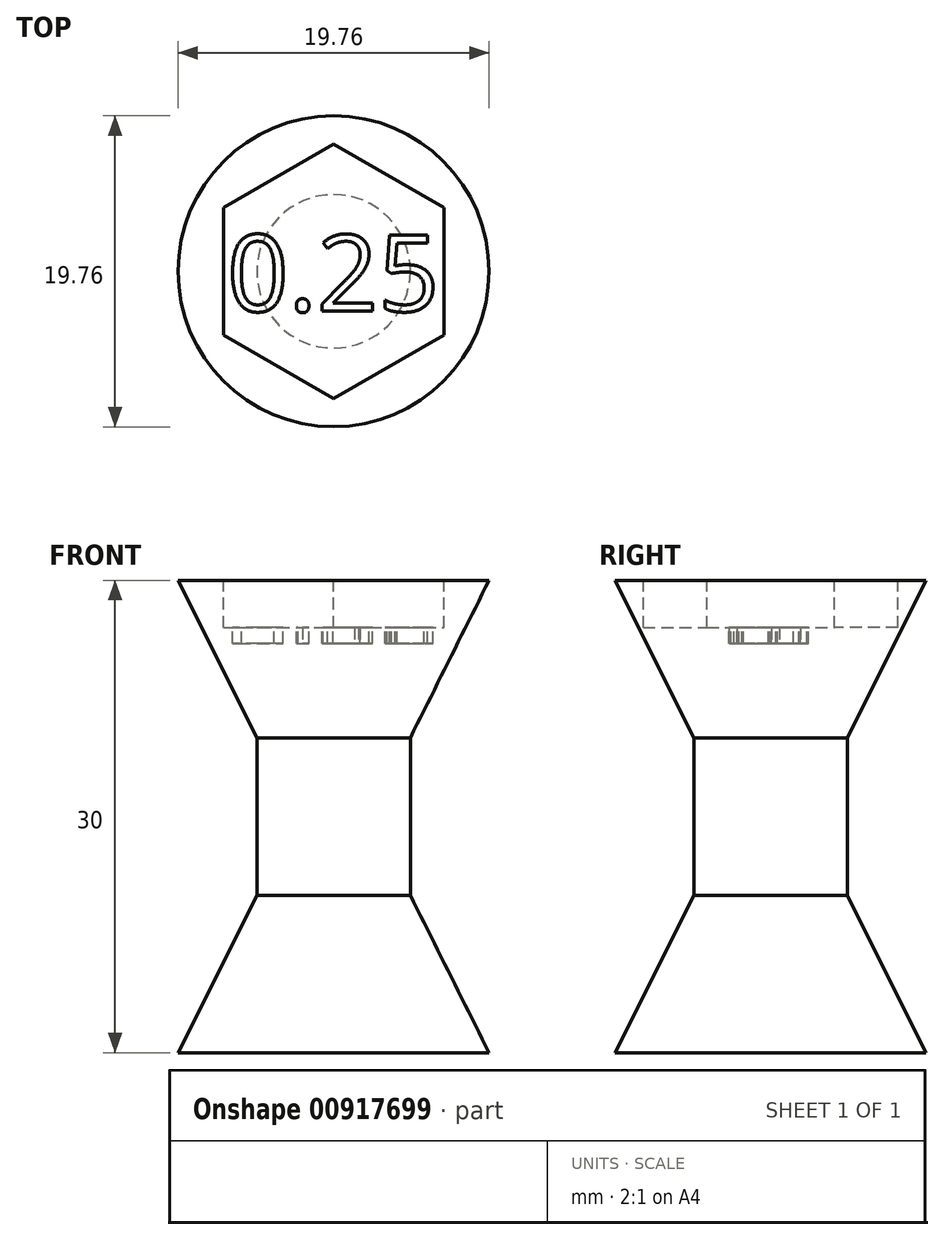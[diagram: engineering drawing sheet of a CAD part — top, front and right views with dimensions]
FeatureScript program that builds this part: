
annotation { "Feature Type Name" : "Feature", "Feature Type Description" : "" }
export const myFeature = defineFeature(function(context is Context, id is Id, definition is map)
    precondition{}
    {
        {
            var Q0;
            Q0=qCreatedBy(makeId("Front.planeOp"),FACE);
            var sketch = newSketch(context, id + "F0", { "sketchPlane" : qUnion([Q0])});
            skLineSegment(sketch, "E0", {"start": v(0, 15) * mm, "end": v(0, -15) * mm});
            skLineSegment(sketch, "E1", {"start": v(0, -15) * mm, "end": v(9.88, -15) * mm});
            skLineSegment(sketch, "E2", {"start": v(9.88, -15) * mm, "end": v(4.88, -5) * mm});
            skLineSegment(sketch, "E3", {"start": v(4.88, -5) * mm, "end": v(4.88, 5) * mm});
            skLineSegment(sketch, "E4", {"start": v(4.87, 5) * mm, "end": v(9.87, 15) * mm});
            skLineSegment(sketch, "E5", {"start": v(9.87, 15) * mm, "end": v(0, 15) * mm});
            skSolve(sketch);
        }
        {
            var Q0;
            Q0=makeQuery(id+"F0.imprint","IMPRINT",FACE,{"disambiguationData":[TD([[makeQuery(id+"F0.imprint","IMPRINT",EDGE,{"derivedFrom":sQuery(id+"F0.wireOp",EDGE,"E0")}),1.0]])]});
            var Q1;
            Q1=sQuery(id+"F0.wireOp",EDGE,"E0");
            var Q2;
            Q2=sQuery(id+"F0.wireOp",EDGE,"E1");
            var Q3;
            Q3=sQuery(id+"F0.wireOp",EDGE,"E2");
            var Q4;
            Q4=sQuery(id+"F0.wireOp",EDGE,"E3");
            var Q5;
            Q5=sQuery(id+"F0.wireOp",EDGE,"E4");
            var Q6;
            Q6=sQuery(id+"F0.wireOp",EDGE,"E5");
            var Q7;
            Q7=sQuery(id+"F0.wireOp",EDGE,"E0");
            revolve(context, id + "F1", {"surfaceOperationType" : NewSurfaceOperationType.ADD, "entities" : qUnion([Q0]), "surfaceEntities" : qUnion([Q1, Q2, Q3, Q4, Q5, Q6]), "axis" : qUnion([Q7]), "revolveType" : RevolveType.FULL});
        }
        {
            var Q0;
            Q0=makeQuery(id+"F1.opRevolve","SWEPT_FACE",FACE,{"disambiguationData":[OSD([sQuery(id+"F0.wireOp",EDGE,"E5")])]});
            var sketch = newSketch(context, id + "F2", { "sketchPlane" : qUnion([Q0])});
            skCircle(sketch, "E6.cCircle", {"center": v(0, 0) * mm, "radius": 7 * mm, "construction": true});
            skLineSegment(sketch, "E6.0", {"start": v(0, 8.08) * mm, "end": v(7, 4.04) * mm});
            skLineSegment(sketch, "E6.1", {"start": v(7, 4.04) * mm, "end": v(7, -4.04) * mm});
            skLineSegment(sketch, "E6.2", {"start": v(7, -4.04) * mm, "end": v(0, -8.08) * mm});
            skLineSegment(sketch, "E6.3", {"start": v(0, -8.08) * mm, "end": v(-7, -4.04) * mm});
            skLineSegment(sketch, "E6.4", {"start": v(-7, -4.04) * mm, "end": v(-7, 4.04) * mm});
            skLineSegment(sketch, "E6.5", {"start": v(-7, 4.04) * mm, "end": v(0, 8.08) * mm});
            skPoint(sketch, "E6.0.midPoint", {"position": v(3.5, 6.06) * mm});
            skSolve(sketch);
        }
        {
            var Q0;
            Q0=qSketchRegion(id+"F2",true);
            extrude(context, id + "F3", {"entities" : qUnion([Q0]), "operationType" : NewBodyOperationType.REMOVE, "oppositeDirection" : true, "depth" : 3 * mm, "offsetDistance" : 25 * mm});
        }
        {
            var Q0;
            Q0=makeQuery(id+"F3.boolean.opBoolean","COPY",FACE,{"derivedFrom":makeQuery(id+"F3.opExtrude","CAP_FACE",FACE,{"disambiguationData":[OSD([sQuery(id+"F2.wireOp",EDGE,"E6.0"),sQuery(id+"F2.wireOp",EDGE,"E6.1"),sQuery(id+"F2.wireOp",EDGE,"E6.2"),sQuery(id+"F2.wireOp",EDGE,"E6.3"),sQuery(id+"F2.wireOp",EDGE,"E6.4"),sQuery(id+"F2.wireOp",EDGE,"E6.5")])],"isStart":false})});
            var sketch = newSketch(context, id + "F4", { "sketchPlane" : qUnion([Q0])});
            skText(sketch, "E7", { "text": "0.25", "fontName": "OpenSans-Regular.ttf"});
            const initialGuessF4  = {"E7": [-0.00675, -0.00254, 1, 0, 0.00489]};
            skSetInitialGuess(sketch, initialGuessF4);
            skSolve(sketch);
        }
        {
            var Q0;
            Q0=qSketchRegion(id+"F4",true);
            extrude(context, id + "F5", {"entities" : qUnion([Q0]), "operationType" : NewBodyOperationType.REMOVE, "oppositeDirection" : true, "depth" : 1 * mm, "offsetDistance" : 25 * mm});
        }
    });
